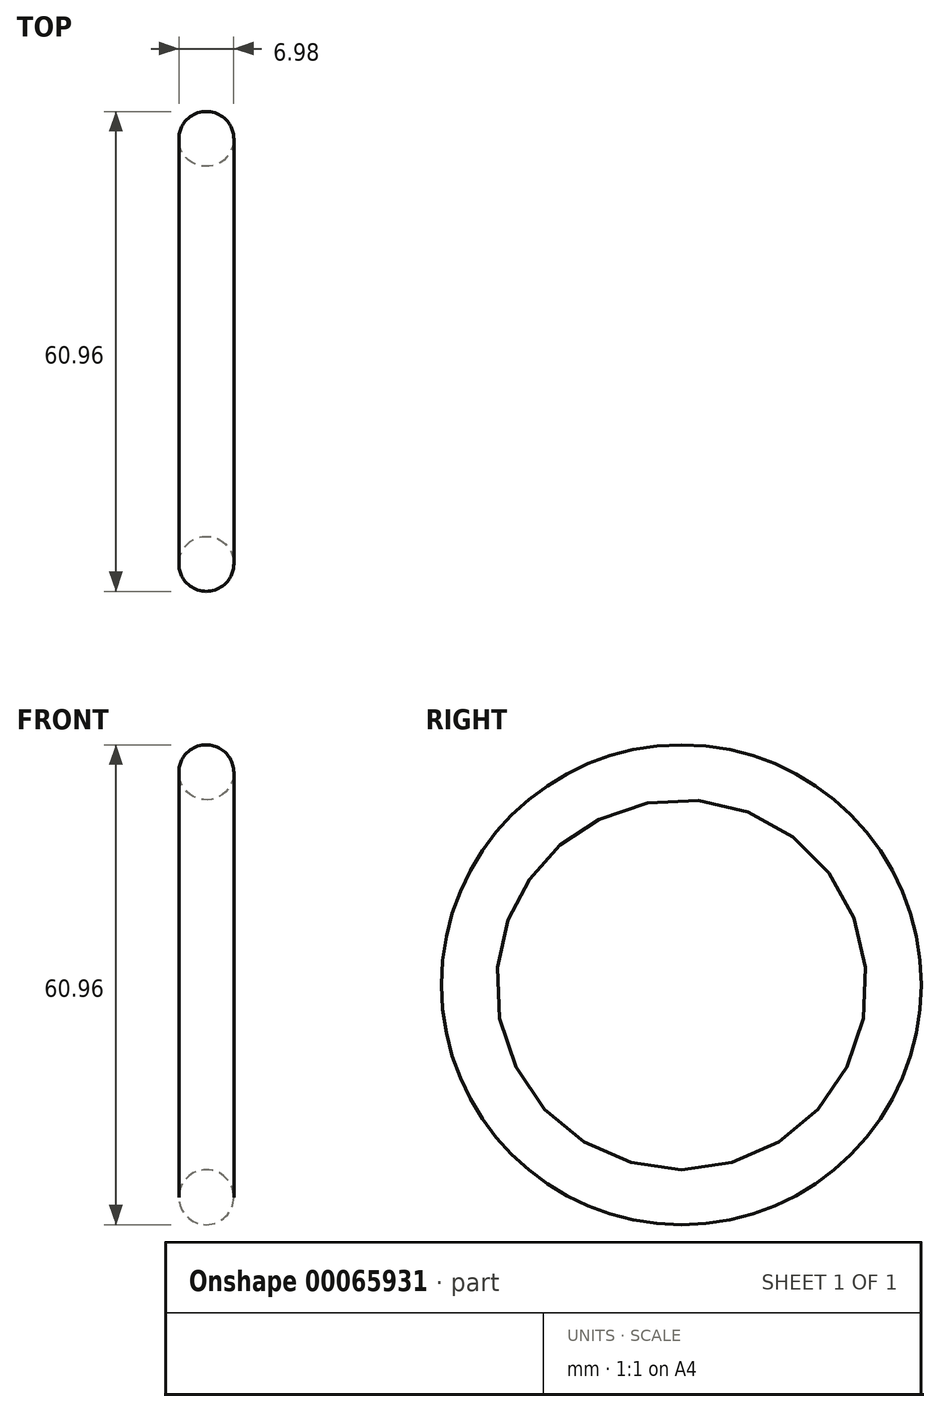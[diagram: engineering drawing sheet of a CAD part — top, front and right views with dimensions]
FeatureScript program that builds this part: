
annotation { "Feature Type Name" : "Feature", "Feature Type Description" : "" }
export const myFeature = defineFeature(function(context is Context, id is Id, definition is map)
    precondition{}
    {
        {
            var Q0;
            Q0=qCreatedBy(makeId("Front.planeOp"),FACE);
            var sketch = newSketch(context, id + "F0", { "sketchPlane" : qUnion([Q0])});
            skLineSegment(sketch, "E0", {"start": v(0, 0) * mm, "end": v(-6.06, 0) * mm, "construction": true});
            skCircle(sketch, "E1", {"center": v(0, 26.99) * mm, "radius": 3.5 * mm});
            skSolve(sketch);
        }
        {
            var Q0;
            Q0=makeQuery(id+"F0.imprint","IMPRINT",FACE,{"disambiguationData":[TD([[makeQuery(id+"F0.imprint","IMPRINT",EDGE,{"derivedFrom":sQuery(id+"F0.wireOp",EDGE,"E1")}),1.0]])]});
            var Q1;
            Q1=sQuery(id+"F0.wireOp",EDGE,"E0");
            revolve(context, id + "F1", {"entities" : qUnion([Q0]), "axis" : qUnion([Q1]), "revolveType" : RevolveType.FULL});
        }
    });
